# Revit family: Bath-Drop_In-Whirlpool-Heater-KOHLER-Consonance-K-1111
name_source: partatom
category: Plumbing Fixtures
units: mm (PartAtom-declared; Revit-internal decimal feet)

## family parameters
Cut with Voids When Loaded = No
Host = Face
OmniClass Number = 23.31.15.00
OmniClass Title = Bathtubs
Part Type = Normal
Room Calculation Point = No
Round Connector Dimension = Use Diameter
Shared = No

## types (1)
- 0-White
    ADA Compliant = No
    Amplifer Electrical Connector = Amplifer Electrical Connector
    Apparent Load = 1800 VA
    Assembly Code = D2010500
    Blower Electrical Connector = Blower Electrical Connector
    CW Connection = No
    Cold Water Inlet = Cold Water Inlet
    Date Modified = 08/16/2022
    Default Elevation = 0"
    Description = 69-1/4 Inch x 69-1/4 Inch drop-in whirlpool bath without jet trim
    Drain Included = No
    Electrical Connector = Yes
    Electrical Note = Two Dedicated Circuit Required
    Finish = KOHLER-Acrylic-0-White
    HW Connection = No
    Heater Electrical Connector = Heater Electrical Connector
    Height = 24"
    Hot Water Inlet = Hot Water Inlet
    Length = 69 1/4"
    Manufacturer = Kohler Co.
    Master Format 2014 = 22 41 19
    Master Format 2014 Name = Residential Bathtubs
    Material = Acrylic
    Model = K-1111-H2-0
    Product Documentation Link = https://www.us.kohler.com
    Product Name = Consonance
    Product Page URL = http://www.us.kohler.com
    Pump Electrical Connector = Pump Electrical Connector
    Type = 1
    URL = https://www.us.kohler.com
    Vent Connection = No
    Voltage = 120 V
    Waste Connection = Yes
    Waste Water Outlet = Waste Water Outlet
    WaterSense Certified = No
    Width = 69 1/4"

## geometry (parser evidence)
native form markers: Sweep x6
no freeform markers — native parametric forms only
